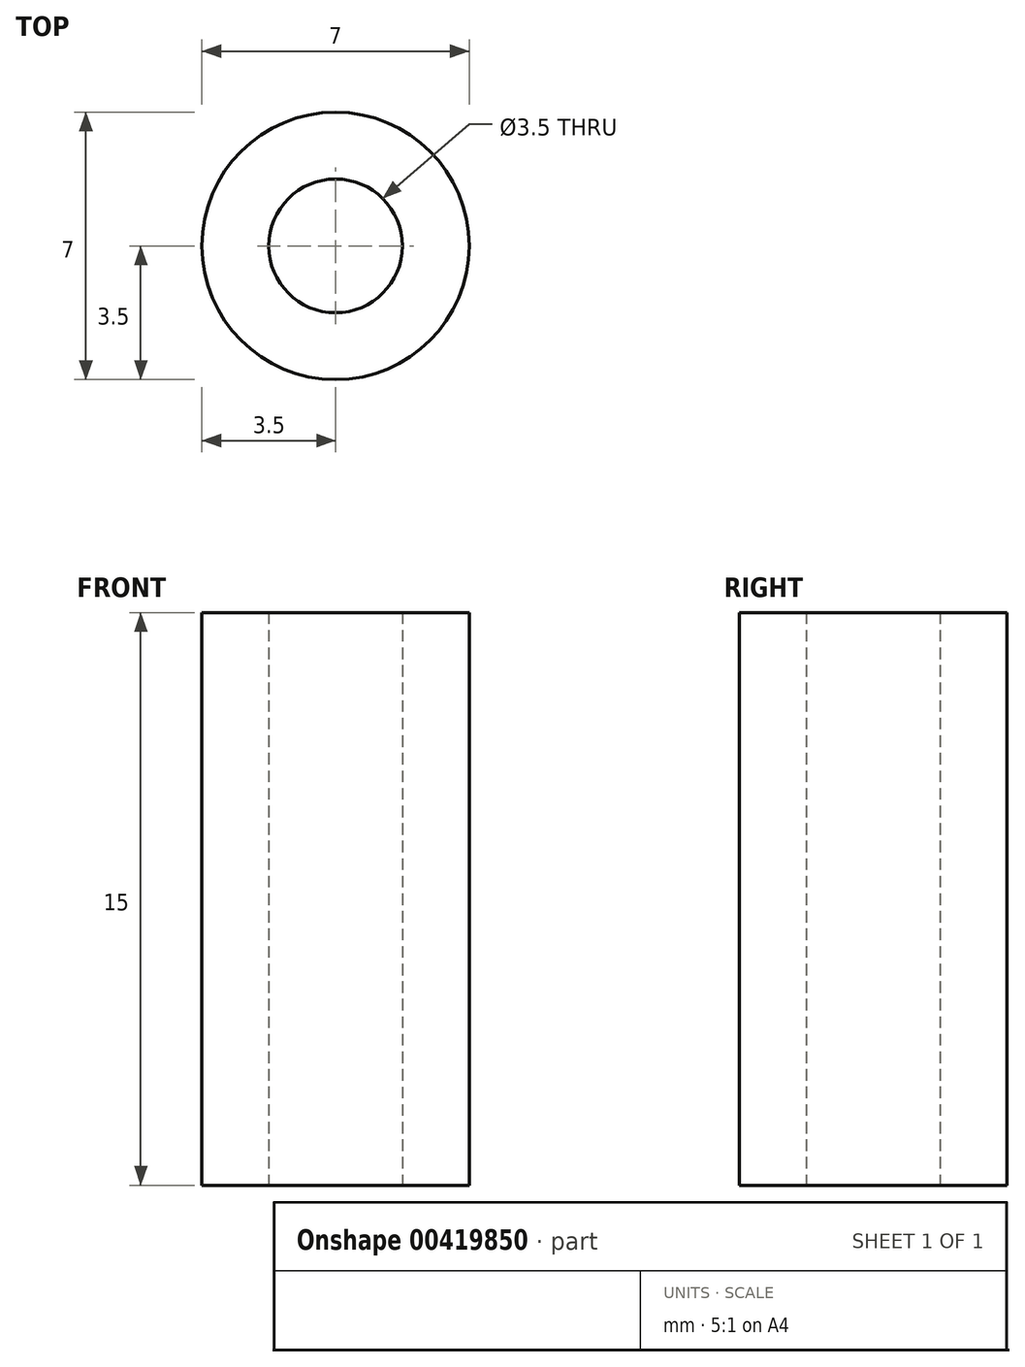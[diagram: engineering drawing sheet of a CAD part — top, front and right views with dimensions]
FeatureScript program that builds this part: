
annotation { "Feature Type Name" : "Feature", "Feature Type Description" : "" }
export const myFeature = defineFeature(function(context is Context, id is Id, definition is map)
    precondition{}
    {
        {
            var Q0;
            Q0=qCreatedBy(makeId("Top.planeOp"),FACE);
            var sketch = newSketch(context, id + "F0", { "sketchPlane" : qUnion([Q0])});
            skCircle(sketch, "E0", {"center": v(0, 0) * mm, "radius": 3.5 * mm});
            skCircle(sketch, "E1", {"center": v(0, 0) * mm, "radius": 1.75 * mm});
            skSolve(sketch);
        }
        {
            var Q0;
            Q0 = qSketchRegion(id + "F0", true);
            extrude(context, id + "F1", {"entities" : qUnion([Q0]), "depth" : 15 * mm});
        }
    });
